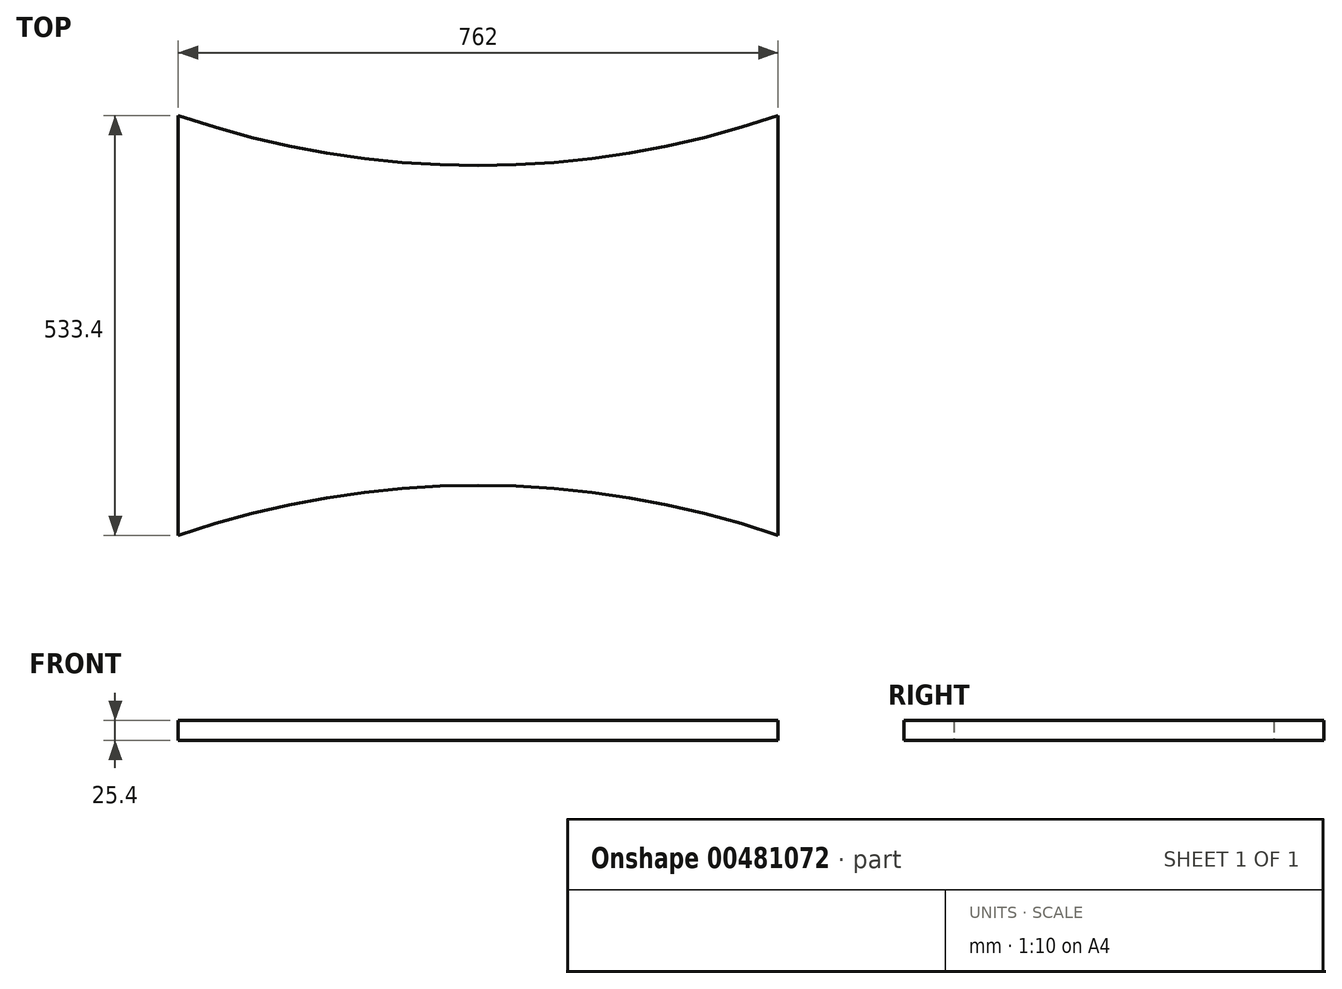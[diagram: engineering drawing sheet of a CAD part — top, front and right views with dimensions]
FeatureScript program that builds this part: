
annotation { "Feature Type Name" : "Feature", "Feature Type Description" : "" }
export const myFeature = defineFeature(function(context is Context, id is Id, definition is map)
    precondition{}
    {
        {
            var Q0;
            Q0=qCreatedBy(makeId("Top.planeOp"),FACE);
            var sketch = newSketch(context, id + "F0", { "sketchPlane" : qUnion([Q0])});
            skLineSegment(sketch, "E0.left", {"start": v(0, 0) * mm, "end": v(0, 533.4) * mm});
            skLineSegment(sketch, "E0.right", {"start": v(-762, 0) * mm, "end": v(-762, 533.4) * mm});
            skArc(sketch, "E1", {"start": v(0, 0) * mm, "mid": v(-381, 63.5) * mm, "end": v(-762, 0) * mm});
            skLineSegment(sketch, "E2", {"start": v(-762, 266.7) * mm, "end": v(0, 266.7) * mm, "construction": true});
            skArc(sketch, "E3.MirrorCS", {"start": v(0, 533.4) * mm, "mid": v(-381, 469.9) * mm, "end": v(-762, 533.4) * mm});
            skSolve(sketch);
        }
        {
            var Q0;
            Q0 = qSketchRegion(id + "F0", true);
            extrude(context, id + "F1", {"entities" : qUnion([Q0]), "depth" : 25.4 * mm});
        }
    });
